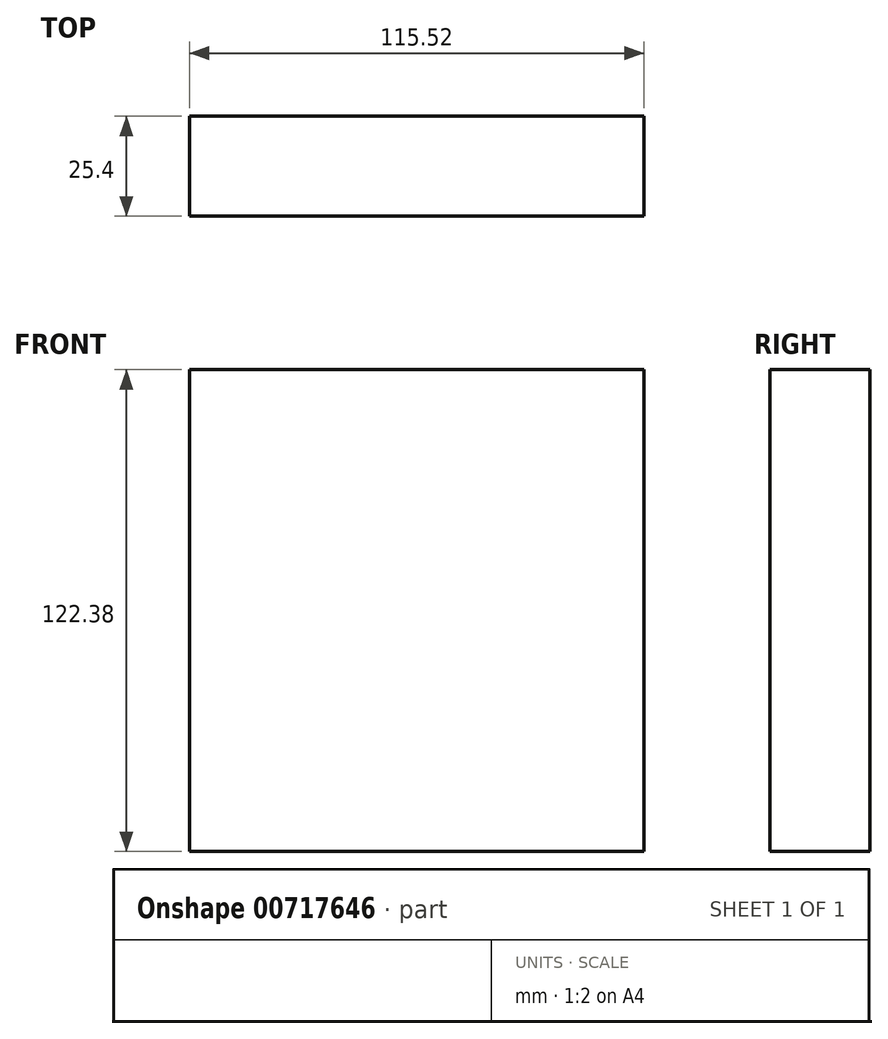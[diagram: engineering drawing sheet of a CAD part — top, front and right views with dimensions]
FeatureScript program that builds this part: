
annotation { "Feature Type Name" : "Feature", "Feature Type Description" : "" }
export const myFeature = defineFeature(function(context is Context, id is Id, definition is map)
    precondition{}
    {
        {
            var Q0;
            Q0=qCreatedBy(makeId("Front.planeOp"),FACE);
            var sketch = newSketch(context, id + "F0", { "sketchPlane" : qUnion([Q0])});
            skLineSegment(sketch, "E0.bottom", {"start": v(-57.12, 60.1) * mm, "end": v(58.4, 60.1) * mm});
            skLineSegment(sketch, "E0.top", {"start": v(-57.12, -62.3) * mm, "end": v(58.4, -62.3) * mm});
            skLineSegment(sketch, "E0.left", {"start": v(-57.12, 60.1) * mm, "end": v(-57.12, -62.3) * mm});
            skLineSegment(sketch, "E0.right", {"start": v(58.4, 60.1) * mm, "end": v(58.4, -62.3) * mm});
            skSolve(sketch);
        }
        {
            var Q0;
            Q0=makeQuery(id+"F0.imprint","IMPRINT",FACE,{"disambiguationData":[TD([[makeQuery(id+"F0.imprint","IMPRINT",EDGE,{"derivedFrom":sQuery(id+"F0.wireOp",EDGE,"E0.bottom")}),-1.0]])]});
            extrude(context, id + "F1", {"entities" : qUnion([Q0]), "oppositeDirection" : true, "depth" : 25.4 * mm, "offsetDistance" : 25.4 * mm});
        }
    });
